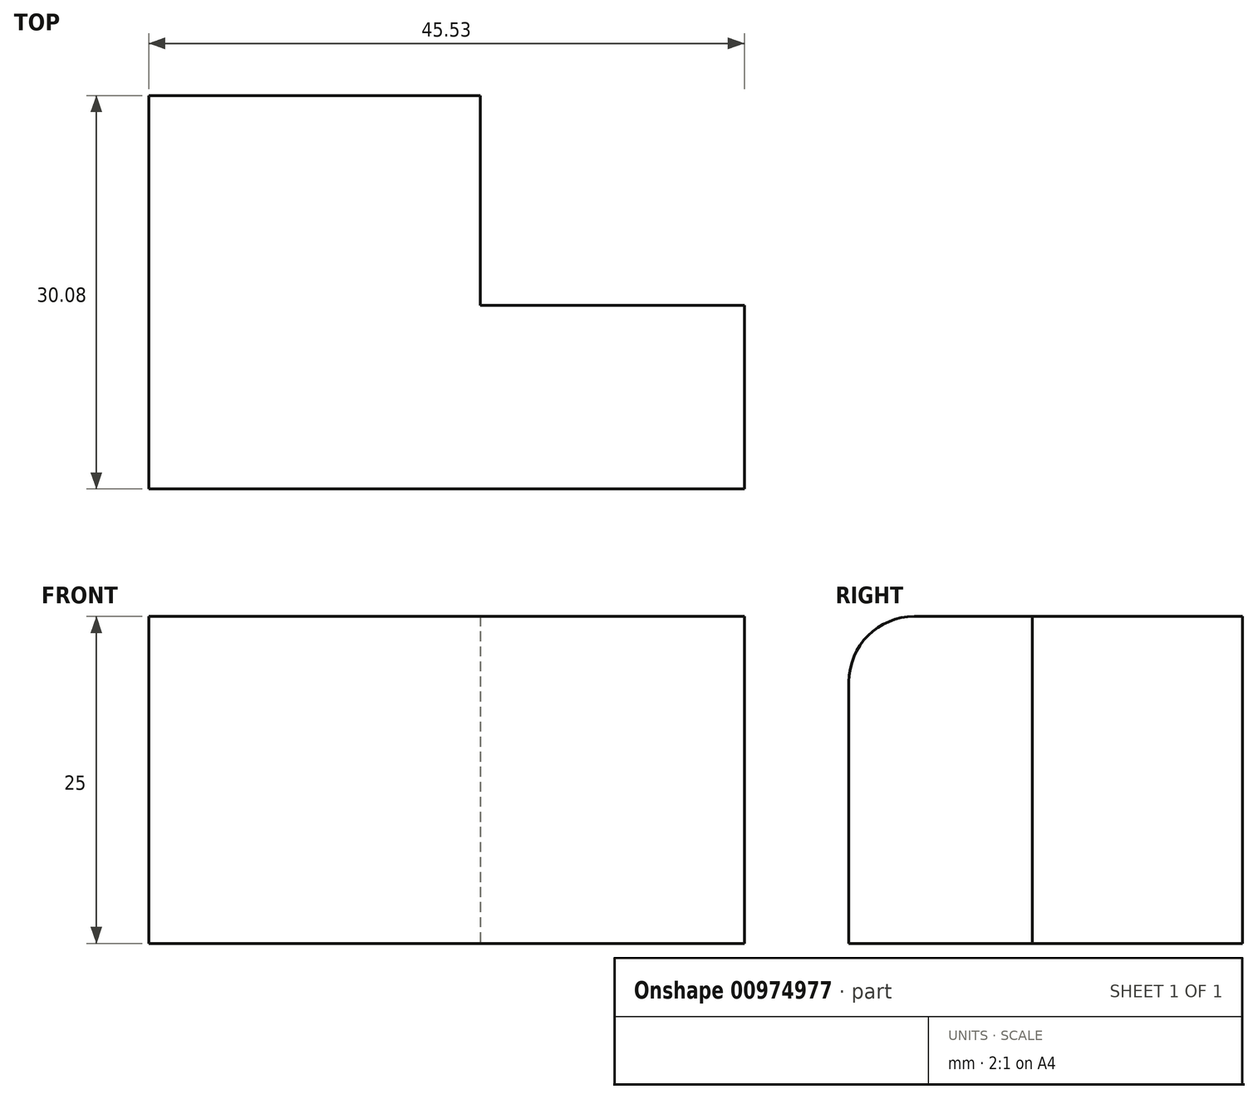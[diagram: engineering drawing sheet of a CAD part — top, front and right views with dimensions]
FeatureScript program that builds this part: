
annotation { "Feature Type Name" : "Feature", "Feature Type Description" : "" }
export const myFeature = defineFeature(function(context is Context, id is Id, definition is map)
    precondition{}
    {
        {
            var Q0;
            Q0=qCreatedBy(makeId("Top.planeOp"),FACE);
            var sketch = newSketch(context, id + "F0", { "sketchPlane" : qUnion([Q0])});
            skLineSegment(sketch, "E0", {"start": v(-34.53, 0) * mm, "end": v(-34.53, -30.08) * mm});
            skLineSegment(sketch, "E1", {"start": v(-34.53, -30.08) * mm, "end": v(11, -30.08) * mm});
            skLineSegment(sketch, "E2", {"start": v(11, -30.08) * mm, "end": v(11, -16.05) * mm});
            skLineSegment(sketch, "E3", {"start": v(11, -16.05) * mm, "end": v(-9.19, -16.05) * mm});
            skLineSegment(sketch, "E4", {"start": v(-9.19, -16.05) * mm, "end": v(-9.19, 0) * mm});
            skLineSegment(sketch, "E5", {"start": v(-9.19, 0) * mm, "end": v(-34.53, 0) * mm});
            skSolve(sketch);
        }
        {
            var Q0;
            Q0=makeQuery(id+"F0.imprint","IMPRINT",FACE,{"disambiguationData":[TD([[makeQuery(id+"F0.imprint","IMPRINT",EDGE,{"derivedFrom":sQuery(id+"F0.wireOp",EDGE,"E0")}),1.0]])]});
            extrude(context, id + "F1", {"entities" : qUnion([Q0]), "depth" : 25 * mm, "offsetDistance" : 25 * mm});
        }
        {
            var Q0;
            Q0=makeQuery(id+"F1.opExtrude","CAP_EDGE",EDGE,{"disambiguationData":[OSD([sQuery(id+"F0.wireOp",EDGE,"E1")])],"isStart":false});
            fillet(context, id + "F2", {"entities" : qUnion([Q0]), "radius" : 5 * mm, "tangentPropagation" : true, "allowEdgeOverflow" : false});
        }
    });
